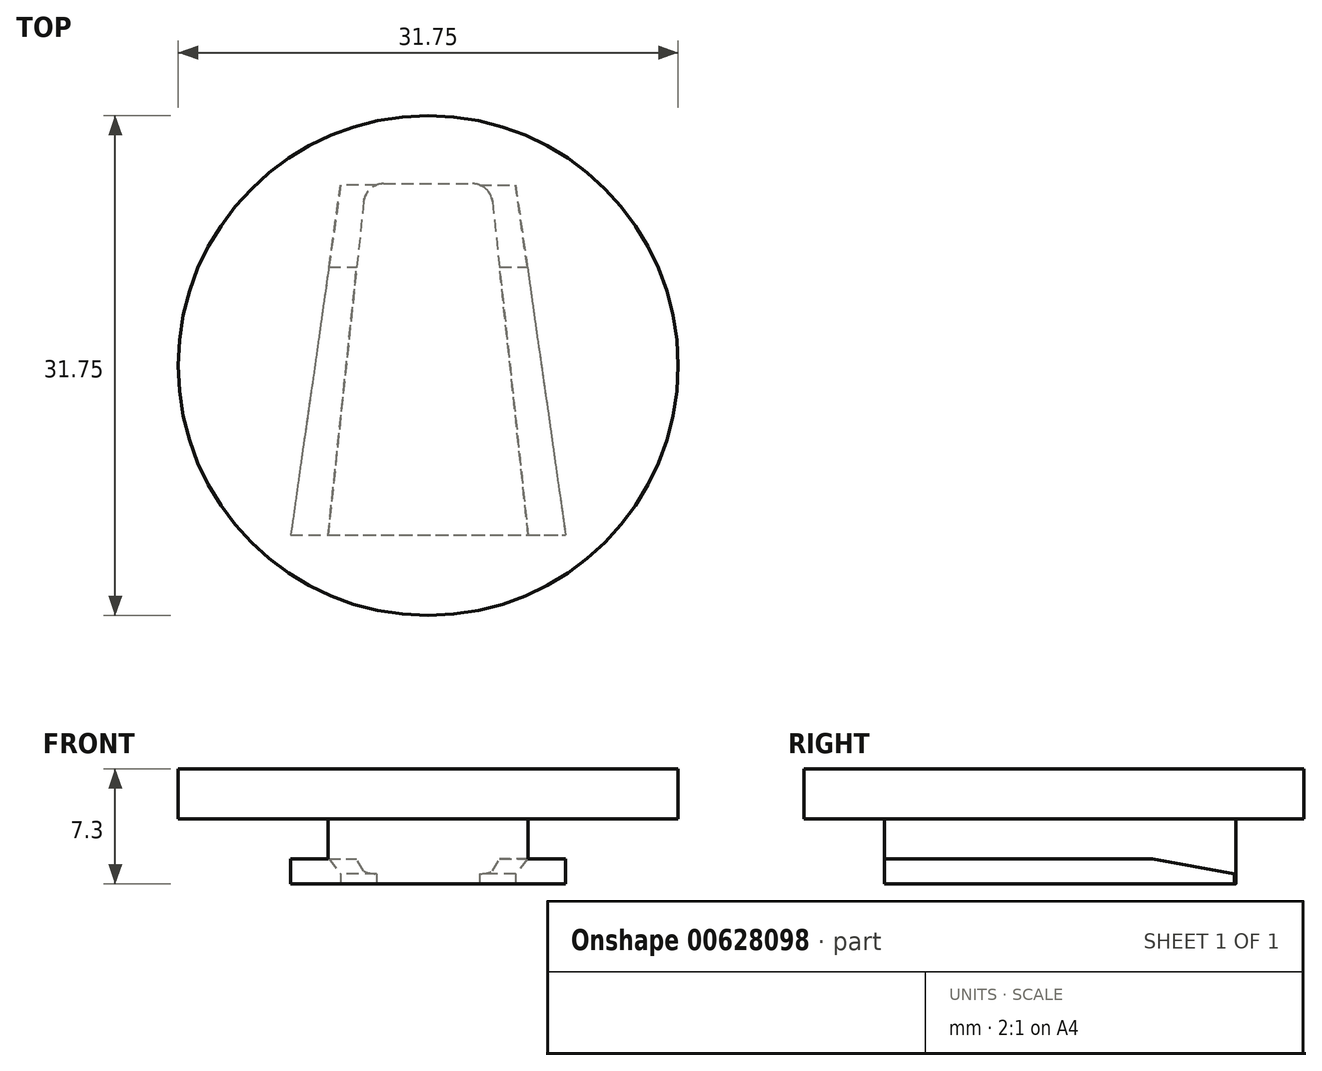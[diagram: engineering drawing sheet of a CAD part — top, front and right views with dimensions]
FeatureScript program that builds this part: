
annotation { "Feature Type Name" : "Feature", "Feature Type Description" : "" }
export const myFeature = defineFeature(function(context is Context, id is Id, definition is map)
    precondition{}
    {
        {
            var Q0;
            Q0=qCreatedBy(makeId("Top.planeOp"),FACE);
            var sketch = newSketch(context, id + "F0", { "sketchPlane" : qUnion([Q0])});
            skLineSegment(sketch, "E0.bottom", {"start": v(0, 0) * mm, "end": v(17.46, 0) * mm});
            skLineSegment(sketch, "E0.top", {"start": v(3.17, 22.23) * mm, "end": v(14.29, 22.23) * mm});
            skLineSegment(sketch, "E1", {"start": v(8.73, 22.23) * mm, "end": v(14.29, 22.23) * mm});
            skLineSegment(sketch, "E2", {"start": v(14.29, 22.23) * mm, "end": v(3.17, 22.23) * mm});
            skLineSegment(sketch, "E3", {"start": v(3.17, 22.23) * mm, "end": v(0, 0) * mm});
            skLineSegment(sketch, "E4", {"start": v(14.29, 22.23) * mm, "end": v(17.46, 0) * mm});
            skPoint(sketch, "E0.left.end.orphan", {"position": v(0, 22.23) * mm});
            skPoint(sketch, "E0.right.end.orphan", {"position": v(17.46, 22.23) * mm});
            skSolve(sketch);
        }
        {
            var Q0;
            Q0=makeQuery(id+"F0.imprint","IMPRINT",FACE,{"disambiguationData":[TD([[makeQuery(id+"F0.imprint","IMPRINT",EDGE,{"derivedFrom":sQuery(id+"F0.wireOp",EDGE,"E0.bottom")}),1.0]])]});
            extrude(context, id + "F1", {"entities" : qUnion([Q0]), "depth" : 1.59 * mm, "offsetDistance" : 25.4 * mm});
        }
        {
            var Q0;
            Q0=qCreatedBy(makeId("Right.planeOp"),FACE);
            var sketch = newSketch(context, id + "F2", { "sketchPlane" : qUnion([Q0])});
            skLineSegment(sketch, "E5", {"start": v(22.23, 0.64) * mm, "end": v(5.84, 3.63) * mm});
            skLineSegment(sketch, "E6", {"start": v(5.84, 3.63) * mm, "end": v(5.84, 7.97) * mm});
            skLineSegment(sketch, "E7", {"start": v(5.84, 7.97) * mm, "end": v(22.72, 7.97) * mm});
            skLineSegment(sketch, "E8", {"start": v(22.72, 7.97) * mm, "end": v(22.23, 0.64) * mm});
            skPoint(sketch, "E9", {"position": v(17.46, 0.68) * mm});
            skSolve(sketch);
        }
        {
            var Q0;
            Q0=makeQuery(id+"F2.imprint","IMPRINT",FACE,{"disambiguationData":[TD([[makeQuery(id+"F2.imprint","IMPRINT",EDGE,{"derivedFrom":sQuery(id+"F2.wireOp",EDGE,"E5")}),-1.0]])]});
            extrude(context, id + "F3", {"entities" : qUnion([Q0]), "operationType" : NewBodyOperationType.REMOVE, "endBound" : BoundingType.THROUGH_ALL, "depth" : 25.4 * mm, "offsetDistance" : 25.4 * mm});
        }
        {
            var Q0;
            Q0=makeQuery(id+"F1.opExtrude","CAP_FACE",FACE,{"disambiguationData":[OSD([sQuery(id+"F0.wireOp",EDGE,"E0.bottom"),sQuery(id+"F0.wireOp",EDGE,"E2"),sQuery(id+"F0.wireOp",EDGE,"E3"),sQuery(id+"F0.wireOp",EDGE,"E4")])],"isStart":false});
            var sketch = newSketch(context, id + "F4", { "sketchPlane" : qUnion([Q0])});
            skLineSegment(sketch, "E10", {"start": v(8.73, 0) * mm, "end": v(15.08, 0) * mm});
            skLineSegment(sketch, "E11", {"start": v(15.08, 0) * mm, "end": v(2.38, 0) * mm});
            skLineSegment(sketch, "E12", {"start": v(8.73, 22.3) * mm, "end": v(5.9, 22.3) * mm});
            skPoint(sketch, "E12.startSnap0", {"position": v(8.73, 17) * mm});
            skLineSegment(sketch, "E13", {"start": v(5.9, 22.3) * mm, "end": v(11.56, 22.3) * mm});
            skLineSegment(sketch, "E14", {"start": v(4.64, 21.17) * mm, "end": v(2.38, 0) * mm});
            skLineSegment(sketch, "E15", {"start": v(12.82, 21.17) * mm, "end": v(15.08, 0) * mm});
            skPoint(sketch, "E16.visualSharp", {"position": v(4.76, 22.3) * mm});
            skArc(sketch, "E16.filletArc", {"start": v(5.9, 22.3) * mm, "mid": v(5.06, 21.98) * mm, "end": v(4.64, 21.17) * mm});
            skPoint(sketch, "E17.visualSharp", {"position": v(12.7, 22.3) * mm});
            skArc(sketch, "E17.filletArc", {"start": v(12.82, 21.17) * mm, "mid": v(12.4, 21.98) * mm, "end": v(11.56, 22.3) * mm});
            skSolve(sketch);
        }
        {
            var Q0;
            Q0 = qSketchRegion(id + "F4", true);
            var Q1;
            Q1=makeQuery(id+"F1.opExtrude","CAP_FACE",FACE,{"disambiguationData":[OSD([sQuery(id+"F0.wireOp",EDGE,"E0.bottom"),sQuery(id+"F0.wireOp",EDGE,"E2"),sQuery(id+"F0.wireOp",EDGE,"E3"),sQuery(id+"F0.wireOp",EDGE,"E4")])],"isStart":true});
            extrude(context, id + "F5", {"entities" : qUnion([Q0]), "operationType" : NewBodyOperationType.ADD, "depth" : 2.54 * mm, "offsetDistance" : 25.4 * mm, "hasSecondDirection" : true, "secondDirectionBound" : SecondDirectionBoundingType.UP_TO_SURFACE, "secondDirectionOppositeDirection" : true, "secondDirectionDepth" : 25.4 * mm, "secondDirectionBoundEntityFace" : qUnion([Q1])});
        }
        {
            var Q0;
            Q0=makeQuery(id+"F5.opExtrude","CAP_FACE",FACE,{"disambiguationData":[OSD([sQuery(id+"F4.wireOp",EDGE,"E11"),sQuery(id+"F4.wireOp",EDGE,"E13"),sQuery(id+"F4.wireOp",EDGE,"E14"),sQuery(id+"F4.wireOp",EDGE,"E15"),sQuery(id+"F4.wireOp",EDGE,"E16.filletArc"),sQuery(id+"F4.wireOp",EDGE,"E17.filletArc")])],"isStart":false});
            var sketch = newSketch(context, id + "F6", { "sketchPlane" : qUnion([Q0])});
            skPoint(sketch, "E18", {"position": v(8.73, 10.75) * mm});
            skPoint(sketch, "E18.positionSnap0", {"position": v(8.73, 0) * mm});
            skCircle(sketch, "E19", {"center": v(8.73, 10.75) * mm, "radius": 15.88 * mm});
            skSolve(sketch);
        }
        {
            var Q0;
            Q0 = qSketchRegion(id + "F6", true);
            extrude(context, id + "F7", {"entities" : qUnion([Q0]), "operationType" : NewBodyOperationType.ADD, "depth" : 3.17 * mm, "offsetDistance" : 25.4 * mm});
        }
    });
